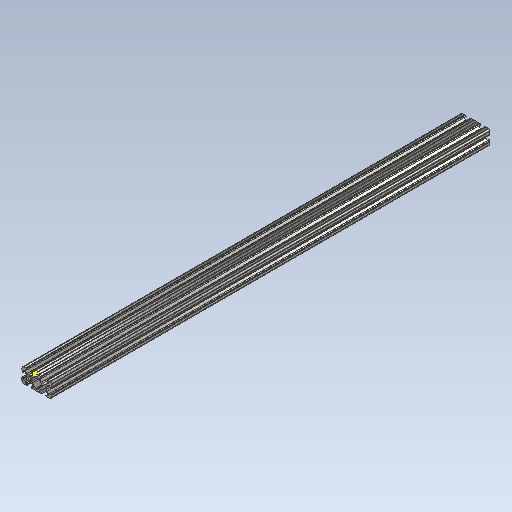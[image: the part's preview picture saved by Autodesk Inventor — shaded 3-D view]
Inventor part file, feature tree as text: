
AUTODESK INVENTOR PART (.ipt)
format: ipt  version: 2020 (Build 240168000, 168)  size: 389,120 bytes
history: native  units: in
note: dims shown in document units (in); Inventor stores cm internally (conversion verified against a paired STEP export)
features: other x3, sketch x2
ambient origin geometry x8: Origin, YZ Plane, XZ Plane, XY Plane, X Axis, Y Axis, Z Axis, Center Point
bodies: Solid1 (feature_tree)
feature tree (5):
  other  "25in 2x1 T Slot.ipt"
  other  "Solid1::25in 2x1 T Slot.ipt"
  other  "TaggingFeature1"
  sketch  "Sketch1"  dims[d0=0.3937in]
  sketch  "Sketch2"
